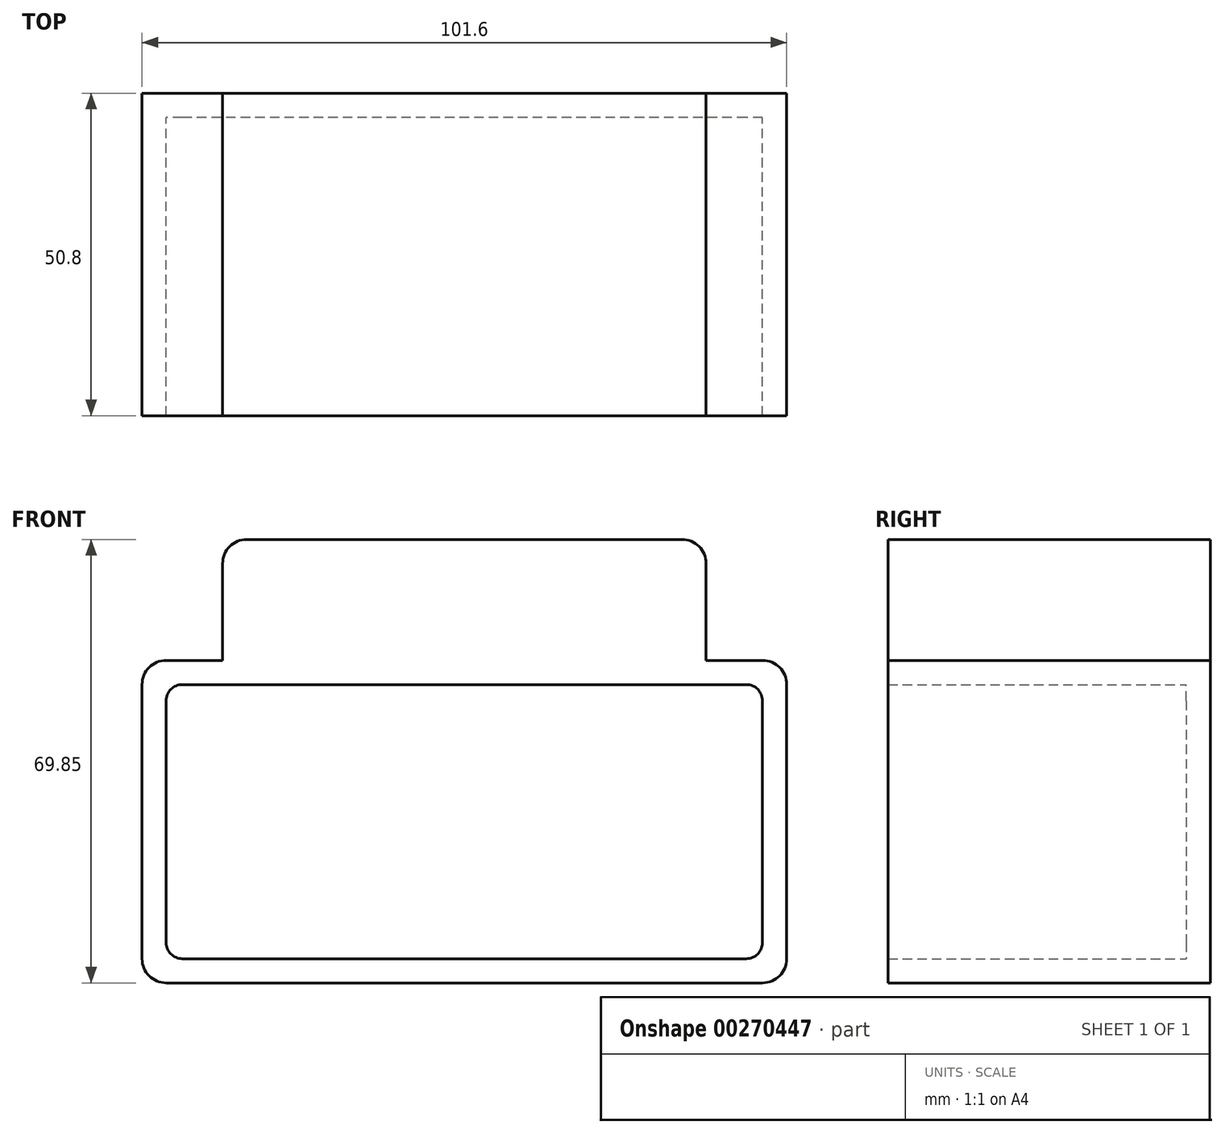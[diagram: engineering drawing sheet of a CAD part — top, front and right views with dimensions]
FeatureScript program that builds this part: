
annotation { "Feature Type Name" : "Feature", "Feature Type Description" : "" }
export const myFeature = defineFeature(function(context is Context, id is Id, definition is map)
    precondition{}
    {
        {
            var Q0;
            Q0=qCreatedBy(makeId("Front.planeOp"),FACE);
            var sketch = newSketch(context, id + "F0", { "sketchPlane" : qUnion([Q0])});
            skLineSegment(sketch, "E0.bottom", {"start": v(47, 25.4) * mm, "end": v(-46.99, 25.4) * mm});
            skLineSegment(sketch, "E0.top", {"start": v(47, -25.4) * mm, "end": v(-47, -25.4) * mm});
            skLineSegment(sketch, "E0.left", {"start": v(50.8, 21.59) * mm, "end": v(50.8, -21.59) * mm});
            skLineSegment(sketch, "E0.right", {"start": v(-50.8, 21.59) * mm, "end": v(-50.8, -21.59) * mm});
            skPoint(sketch, "E0.middle", {"position": v(0, 0) * mm});
            skPoint(sketch, "E1.endSnap0", {"position": v(0, 25.4) * mm});
            skLineSegment(sketch, "E2", {"start": v(0, 44.45) * mm, "end": v(34.3, 44.45) * mm});
            skLineSegment(sketch, "E3", {"start": v(0, 44.45) * mm, "end": v(-34.3, 44.45) * mm});
            skLineSegment(sketch, "E4", {"start": v(-38.1, 40.64) * mm, "end": v(-38.1, 25.4) * mm});
            skLineSegment(sketch, "E5", {"start": v(38.1, 40.64) * mm, "end": v(38.1, 25.4) * mm});
            skPoint(sketch, "E6.visualSharp", {"position": v(-50.8, 25.4) * mm});
            skArc(sketch, "E6.filletArc", {"start": v(-46.99, 25.4) * mm, "mid": v(-49.68, 24.28) * mm, "end": v(-50.8, 21.59) * mm});
            skPoint(sketch, "E7.visualSharp", {"position": v(-50.8, -25.4) * mm});
            skArc(sketch, "E7.filletArc", {"start": v(-50.8, -21.59) * mm, "mid": v(-49.68, -24.28) * mm, "end": v(-47, -25.4) * mm});
            skPoint(sketch, "E8.visualSharp", {"position": v(50.8, -25.4) * mm});
            skArc(sketch, "E8.filletArc", {"start": v(47, -25.4) * mm, "mid": v(49.68, -24.28) * mm, "end": v(50.8, -21.59) * mm});
            skPoint(sketch, "E9.visualSharp", {"position": v(50.8, 25.4) * mm});
            skArc(sketch, "E9.filletArc", {"start": v(50.8, 21.59) * mm, "mid": v(49.68, 24.28) * mm, "end": v(47, 25.4) * mm});
            skPoint(sketch, "E10.visualSharp", {"position": v(38.1, 44.45) * mm});
            skArc(sketch, "E10.filletArc", {"start": v(38.1, 40.64) * mm, "mid": v(36.98, 43.33) * mm, "end": v(34.3, 44.45) * mm});
            skPoint(sketch, "E11.visualSharp", {"position": v(-38.1, 44.45) * mm});
            skArc(sketch, "E11.filletArc", {"start": v(-34.3, 44.45) * mm, "mid": v(-36.98, 43.33) * mm, "end": v(-38.1, 40.64) * mm});
            skSolve(sketch);
        }
        {
            var Q0;
            Q0=makeQuery(id+"F0.imprint","IMPRINT",FACE,{"disambiguationData":[TD([[makeQuery(id+"F0.imprint","IMPRINT",EDGE,{"derivedFrom":sQuery(id+"F0.wireOp",EDGE,"E0.top")}),-1.0]])]});
            extrude(context, id + "F1", {"entities" : qUnion([Q0]), "depth" : 50.8 * mm});
        }
        {
            var Q0;
            Q0=makeQuery(id+"F1.opExtrude","CAP_FACE",FACE,{"disambiguationData":[OSD([sQuery(id+"F0.wireOp",EDGE,"E0.bottom"),sQuery(id+"F0.wireOp",EDGE,"E0.top"),sQuery(id+"F0.wireOp",EDGE,"E0.left"),sQuery(id+"F0.wireOp",EDGE,"E0.right"),sQuery(id+"F0.wireOp",EDGE,"E6.filletArc"),sQuery(id+"F0.wireOp",EDGE,"E7.filletArc"),sQuery(id+"F0.wireOp",EDGE,"E8.filletArc"),sQuery(id+"F0.wireOp",EDGE,"E9.filletArc")])],"isStart":false});
            shell(context, id + "F2", {"entities" : qUnion([Q0]), "thickness" : 3.8 * mm});
        }
        {
            var Q0;
            Q0=makeQuery(id+"F2.opShell","OFFSET_EDGE",EDGE,{"disambiguationData":[OSD([sQuery(id+"F0.wireOp",EDGE,"E0.bottom"),sQuery(id+"F0.wireOp",EDGE,"E0.right"),sQuery(id+"F0.wireOp",EDGE,"E6.filletArc")])]});
            var Q1;
            Q1=makeQuery(id+"F2.opShell","OFFSET_EDGE",EDGE,{"disambiguationData":[OSD([sQuery(id+"F0.wireOp",EDGE,"E0.top"),sQuery(id+"F0.wireOp",EDGE,"E0.right"),sQuery(id+"F0.wireOp",EDGE,"E7.filletArc")])]});
            var Q2;
            Q2=makeQuery(id+"F2.opShell","OFFSET_EDGE",EDGE,{"disambiguationData":[OSD([sQuery(id+"F0.wireOp",EDGE,"E0.top"),sQuery(id+"F0.wireOp",EDGE,"E0.left"),sQuery(id+"F0.wireOp",EDGE,"E8.filletArc")])]});
            var Q3;
            Q3=makeQuery(id+"F2.opShell","OFFSET_EDGE",EDGE,{"disambiguationData":[OSD([sQuery(id+"F0.wireOp",EDGE,"E0.bottom"),sQuery(id+"F0.wireOp",EDGE,"E0.left"),sQuery(id+"F0.wireOp",EDGE,"E9.filletArc")])]});
            fillet(context, id + "F3", {"entities" : qUnion([Q0, Q1, Q2, Q3]), "radius" : 2.54 * mm, "tangentPropagation" : true, "allowEdgeOverflow" : false});
        }
        {
            var Q0;
            Q0=makeQuery(id+"F0.imprint","IMPRINT",FACE,{"disambiguationData":[TD([[makeQuery(id+"F0.imprint","IMPRINT",EDGE,{"derivedFrom":sQuery(id+"F0.wireOp",EDGE,"E2")}),-1.0]])]});
            extrude(context, id + "F4", {"entities" : qUnion([Q0]), "operationType" : NewBodyOperationType.ADD, "depth" : 50.8 * mm});
        }
    });
